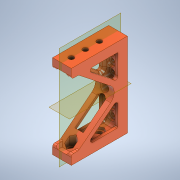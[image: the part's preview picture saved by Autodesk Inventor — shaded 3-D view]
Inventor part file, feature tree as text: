
AUTODESK INVENTOR PART (.ipt)
format: ipt  version: 2020 (Build 240168000, 168)  size: 693,248 bytes
history: native  units: in
note: dims shown in document units (in); Inventor stores cm internally (conversion verified against a paired STEP export)
features: extrude x14, sketch x12, projected_geometry x8, fillet x5, plane x5, chamfer x2, mirror x1
ambient origin geometry x8: Origin, YZ Plane, XZ Plane, XY Plane, X Axis, Y Axis, Z Axis, Center Point
bodies: Solid1 (feature_tree)
feature tree (47):
  extrude  "Extrusion1"  Depth=4.5in
  extrude  "Extrusion2"  Depth=0.5in
  fillet  "Fillet1"  Radius=0.5in
  extrude  "Extrusion3"  Depth=0.25in
  fillet  "Fillet2"  Radius=0.25in
  extrude  "Extrusion4"  Depth=0.5in
  plane  "Work Plane1"
  extrude  "Extrusion5"  Depth=2.5in
  extrude  "Extrusion6"  TaperAngle=0.0deg  [1 undecoded]
  plane  "Work Plane2"
  extrude  "Extrusion7"  Depth=0.4532in
  plane  "Work Plane3"
  extrude  "Extrusion8"  Depth=0.25in TaperAngle=0.0deg
  extrude  "Extrusion10"  Depth=0.5in
  plane  "Work Plane4"
  plane  "Work Plane5"
  extrude  "Extrusion11"  Depth=0.3937in
  chamfer  "Chamfer1"  [1 undecoded]
  extrude  "Extrusion12"  Depth=0.4532in
  extrude  "Extrusion13"  [1 undecoded]
  chamfer  "Chamfer2"  Distance=0.4532in
  fillet  "Fillet3"  Radius=2.5in
  fillet  "Fillet4"  Radius=0.375in
  extrude  "Extrusion14"  Depth=0.125in TaperAngle=0.0deg
  extrude  "Extrusion15"  [1 undecoded]
  mirror  "Mirror2"
  fillet  "Fillet5"  Radius=0.375in
  sketch  "Sketch1"  dims[d0=1.0in d1=4.5in]
  sketch  "Sketch2"  dims[d2=3.0in d3=0.0in d4=0.5in d5=0.5in]
  sketch  "Sketch3"  dims[d6=0.0in d7=0.0in d8=0.05in d9=0.25in]
  sketch  "Sketch4"  dims[d10=1.0in d11=0.0in d12=0.5in d13=0.125in]
  sketch  "Sketch6"  dims[d14=0.2in d16=2.5in]
  sketch  "Sketch8"  dims[d17=4.3307in d19=0.5in d20=0.3937in d22=1.0in d24=0.0in d25=0.0in]
  sketch  "Sketch10"  dims[d26=-0.25in d27=0.4532in]
  sketch  "Sketch11"  dims[d28=3.5433in d30=0.5in d31=0.3937in d33=1.0in d35=0.25in d36=0.0in]
  sketch  "Sketch12"  dims[d37=1.0in d38=0.5in]
  projected_geometry  "Projected Loop1"
  projected_geometry  "Projected Loop2"
  projected_geometry  "Projected Loop3"
  sketch  "Sketch13"  dims[d39=0.2656in d40=1.1811in d42=0.75in d43=0.3937in d45=1.0in d47=0.0in d48=0.0in]
  projected_geometry  "Projected Loop4"
  projected_geometry  "Projected Loop5"
  projected_geometry  "Projected Loop6"
  sketch  "Sketch14"  dims[d49=-0.25in d50=0.4532in]
  sketch  "Sketch15"  dims[d51=2.5in d52=0.0in d53=-0.25in d54=0.4532in d55=2.5in d56=0.0in d59=0.375in d60=0.26in d61=0.0in d62=-0.5in d63=0.375in d64=0.375in d65=0.375in d66=0.4532in d67=0.0in d68=0.125in d69=0.125in d70=45.0deg d71=0.4532in d72=0.0in d73=0.975in d74=0.0in d75=0.125in d76=0.125in d77=45.0deg d78=0.125in d79=0.175in d80=1.0in d81=0.0in d82=1.0in d83=0.0in d84=0.0782in]
  projected_geometry  "Projected Loop7"
  projected_geometry  "Projected Loop8"
note: 4 required parameter values undecoded (feature->parameter linkage not recoverable at this tier; creation-order binding heuristic only, values carry confidence <= 0.55)
